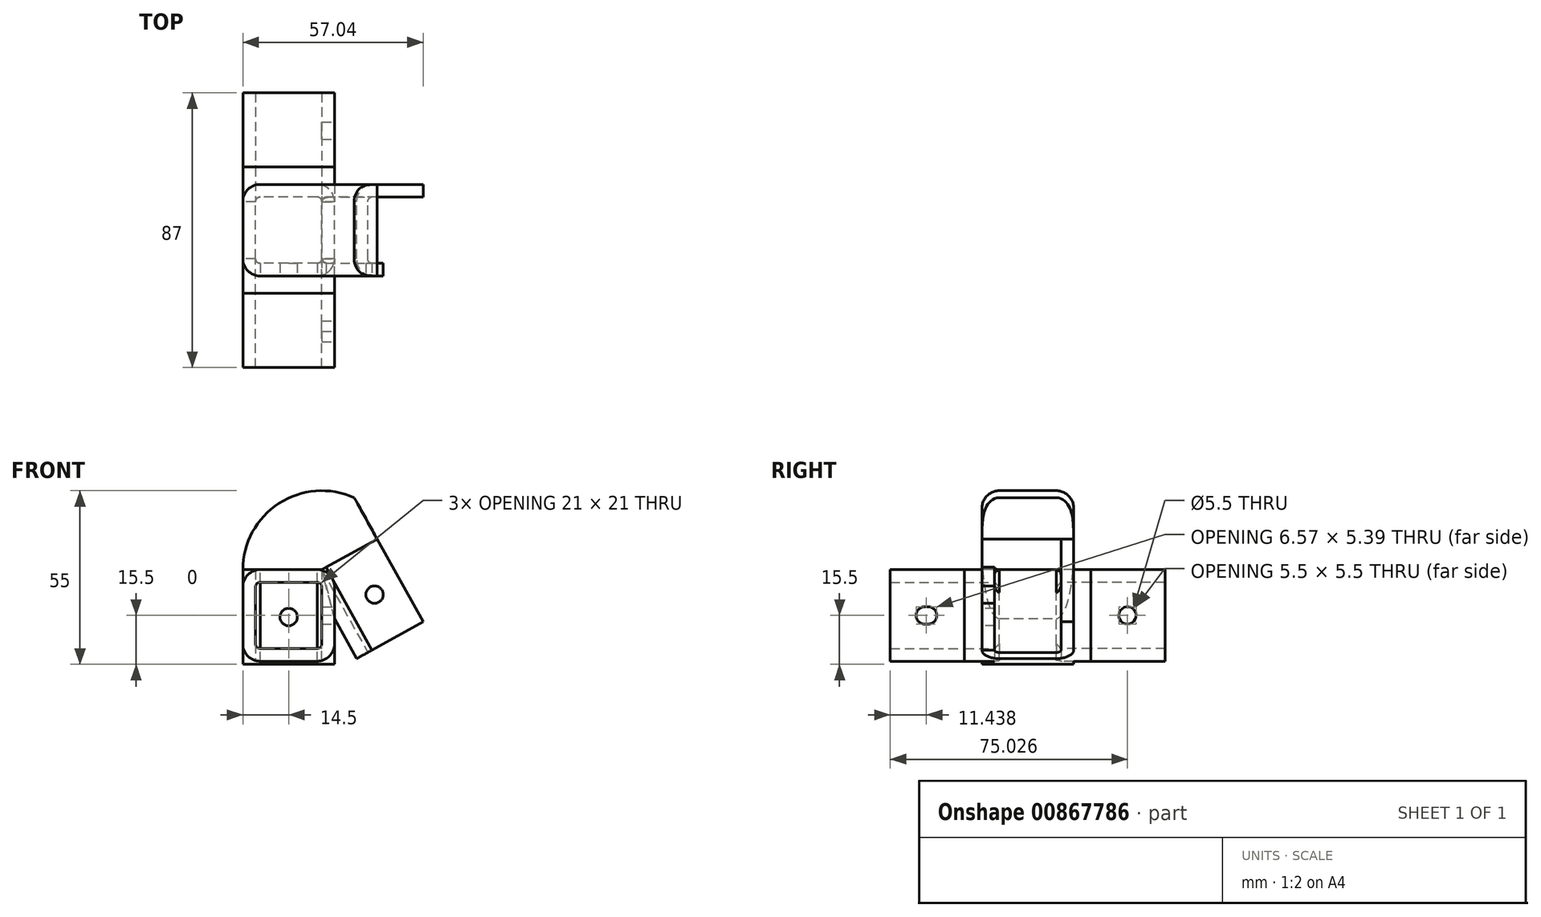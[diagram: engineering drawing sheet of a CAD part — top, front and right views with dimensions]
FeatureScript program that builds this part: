
annotation { "Feature Type Name" : "Feature", "Feature Type Description" : "" }
export const myFeature = defineFeature(function(context is Context, id is Id, definition is map)
    precondition{}
    {
        {
            var Q0;
            Q0=qCreatedBy(makeId("Top.planeOp"),FACE);
            var sketch = newSketch(context, id + "F0", { "sketchPlane" : qUnion([Q0])});
            skLineSegment(sketch, "E0.bottom", {"start": v(-1.5, 0) * mm, "end": v(-19.5, 0) * mm});
            skLineSegment(sketch, "E0.top", {"start": v(-1.5, 21) * mm, "end": v(-19.5, 21) * mm});
            skLineSegment(sketch, "E0.left", {"start": v(0, 1.5) * mm, "end": v(0, 19.5) * mm});
            skLineSegment(sketch, "E0.right", {"start": v(-21, 1.5) * mm, "end": v(-21, 19.5) * mm});
            skPoint(sketch, "E1.visualSharp", {"position": v(-21, 21) * mm});
            skArc(sketch, "E1.filletArc", {"start": v(-19.5, 21) * mm, "mid": v(-20.56, 20.56) * mm, "end": v(-21, 19.5) * mm});
            skPoint(sketch, "E2.visualSharp", {"position": v(0, 21) * mm});
            skArc(sketch, "E2.filletArc", {"start": v(0, 19.5) * mm, "mid": v(-0.44, 20.56) * mm, "end": v(-1.5, 21) * mm});
            skPoint(sketch, "E3.visualSharp", {"position": v(0, 0) * mm});
            skArc(sketch, "E3.filletArc", {"start": v(-1.5, 0) * mm, "mid": v(-0.44, 0.44) * mm, "end": v(0, 1.5) * mm});
            skPoint(sketch, "E4.visualSharp", {"position": v(-21, 0) * mm});
            skArc(sketch, "E4.filletArc", {"start": v(-21, 1.5) * mm, "mid": v(-20.56, 0.44) * mm, "end": v(-19.5, 0) * mm});
            skArc(sketch, "E5.0", {"start": v(4, 19.5) * mm, "mid": v(2.39, 23.39) * mm, "end": v(-1.5, 25) * mm});
            skLineSegment(sketch, "E5.1", {"start": v(4, 1.5) * mm, "end": v(4, 19.5) * mm});
            skLineSegment(sketch, "E5.2", {"start": v(-1.5, 25) * mm, "end": v(-19.5, 25) * mm});
            skArc(sketch, "E5.3", {"start": v(-1.5, -4) * mm, "mid": v(2.39, -2.39) * mm, "end": v(4, 1.5) * mm});
            skArc(sketch, "E5.4", {"start": v(-19.5, 25) * mm, "mid": v(-23.39, 23.39) * mm, "end": v(-25, 19.5) * mm});
            skLineSegment(sketch, "E5.5", {"start": v(-25, 1.5) * mm, "end": v(-25, 19.5) * mm});
            skArc(sketch, "E5.6", {"start": v(-25, 1.5) * mm, "mid": v(-23.39, -2.39) * mm, "end": v(-19.5, -4) * mm});
            skLineSegment(sketch, "E5.7", {"start": v(-1.5, -4) * mm, "end": v(-19.5, -4) * mm});
            skSolve(sketch);
        }
        {
            var Q0;
            Q0=makeQuery(id+"F0.imprint","IMPRINT",FACE,{"disambiguationData":[TD([[makeQuery(id+"F0.imprint","IMPRINT",EDGE,{"derivedFrom":sQuery(id+"F0.wireOp",EDGE,"E0.bottom")}),1.0]])]});
            extrude(context, id + "F1", {"entities" : qUnion([Q0]), "oppositeDirection" : true, "depth" : 30 * mm, "offsetDistance" : 25 * mm});
        }
        {
            var Q0;
            Q0=qCreatedBy(makeId("Front.planeOp"),FACE);
            var sketch = newSketch(context, id + "F2", { "sketchPlane" : qUnion([Q0])});
            skLineSegment(sketch, "E6", {"start": v(0, 0) * mm, "end": v(14.54, -26.24) * mm});
            skLineSegment(sketch, "E7", {"start": v(14.54, -26.24) * mm, "end": v(32.04, -16.54) * mm});
            skLineSegment(sketch, "E8", {"start": v(32.04, -16.54) * mm, "end": v(17.5, 9.7) * mm});
            skLineSegment(sketch, "E9", {"start": v(17.5, 9.7) * mm, "end": v(0, 0) * mm});
            skSolve(sketch);
        }
        {
            var Q0;
            Q0=makeQuery(id+"F2.imprint","IMPRINT",FACE,{"disambiguationData":[TD([[makeQuery(id+"F2.imprint","IMPRINT",EDGE,{"derivedFrom":sQuery(id+"F2.wireOp",EDGE,"E6")}),1.0]])]});
            extrude(context, id + "F3", {"entities" : qUnion([Q0]), "operationType" : NewBodyOperationType.ADD, "oppositeDirection" : true, "depth" : 21 * mm, "offsetDistance" : 25 * mm});
        }
        {
            var Q0;
            Q0=makeQuery(id+"F3.opExtrude","SWEPT_FACE",FACE,{"disambiguationData":[OSD([sQuery(id+"F2.wireOp",EDGE,"E7")])]});
            var sketch = newSketch(context, id + "F4", { "sketchPlane" : qUnion([Q0])});
            skLineSegment(sketch, "E10.bottom", {"start": v(20, 0) * mm, "end": v(1.5, 0) * mm});
            skLineSegment(sketch, "E10.top", {"start": v(20, -21) * mm, "end": v(1.5, -21) * mm});
            skLineSegment(sketch, "E10.left", {"start": v(20, 0) * mm, "end": v(20, -21) * mm});
            skLineSegment(sketch, "E10.right", {"start": v(0, -1.5) * mm, "end": v(0, -19.5) * mm});
            skPoint(sketch, "E11.visualSharp", {"position": v(0, 0) * mm});
            skArc(sketch, "E11.filletArc", {"start": v(1.5, 0) * mm, "mid": v(0.44, -0.44) * mm, "end": v(0, -1.5) * mm});
            skPoint(sketch, "E12.visualSharp", {"position": v(0, -21) * mm});
            skArc(sketch, "E12.filletArc", {"start": v(0, -19.5) * mm, "mid": v(0.44, -20.56) * mm, "end": v(1.5, -21) * mm});
            skLineSegment(sketch, "E13.0", {"start": v(20, -25) * mm, "end": v(1.5, -25) * mm});
            skLineSegment(sketch, "E13.1", {"start": v(20, 4) * mm, "end": v(1.5, 4) * mm});
            skArc(sketch, "E13.2", {"start": v(1.5, 4) * mm, "mid": v(-2.39, 2.39) * mm, "end": v(-4, -1.5) * mm});
            skLineSegment(sketch, "E13.3", {"start": v(-4, -1.5) * mm, "end": v(-4, -19.5) * mm});
            skArc(sketch, "E13.4", {"start": v(-4, -19.5) * mm, "mid": v(-2.39, -23.39) * mm, "end": v(1.5, -25) * mm});
            skLineSegment(sketch, "E14", {"start": v(20, 4) * mm, "end": v(20, 0) * mm});
            skLineSegment(sketch, "E15", {"start": v(20, -21) * mm, "end": v(20, -25) * mm});
            skSolve(sketch);
        }
        {
            var Q0;
            {var subQ0=sQuery(id+"F4.wireOp",EDGE,"E10.bottom");Q0=makeQuery(id+"F4.imprint","IMPRINT",FACE,{"disambiguationData":[TD([[makeQuery(id+"F4.imprint","IMPRINT",EDGE,{"derivedFrom":subQ0}),1.0]])]});}
            extrude(context, id + "F5", {"entities" : qUnion([Q0]), "operationType" : NewBodyOperationType.ADD, "oppositeDirection" : true, "depth" : 30 * mm, "offsetDistance" : 25 * mm});
        }
        {
            var Q0;
            {var subQ0=sQuery(id+"F2.wireOp",EDGE,"E7");Q0=makeQuery(id+"F5.boolean.opBoolean","MERGE",FACE,{"derivedFrom":[makeQuery(id+"F3.opExtrude","SWEPT_FACE",FACE,{"disambiguationData":[OSD([subQ0])]}),makeQuery(id+"F5.opExtrude","CAP_FACE",FACE,{"disambiguationData":[OSD([sQuery(id+"F2.wireOp",EDGE,"E6"),subQ0,sQuery(id+"F4.wireOp",EDGE,"E10.bottom"),sQuery(id+"F4.wireOp",EDGE,"E10.top"),sQuery(id+"F4.wireOp",EDGE,"E10.right"),sQuery(id+"F4.wireOp",EDGE,"E13.0"),sQuery(id+"F4.wireOp",EDGE,"E13.1"),sQuery(id+"F4.wireOp",EDGE,"E13.2"),sQuery(id+"F4.wireOp",EDGE,"E13.3"),sQuery(id+"F4.wireOp",EDGE,"E13.4"),sQuery(id+"F4.wireOp",EDGE,"E14"),sQuery(id+"F4.wireOp",EDGE,"E15")])],"isStart":true})]});}
            var sketch = newSketch(context, id + "F6", { "sketchPlane" : qUnion([Q0])});
            skLineSegment(sketch, "E16.bottom", {"start": v(20, 0) * mm, "end": v(1.5, 0) * mm});
            skLineSegment(sketch, "E16.top", {"start": v(20, -21) * mm, "end": v(1.5, -21) * mm});
            skLineSegment(sketch, "E16.left", {"start": v(20, 0) * mm, "end": v(20, -21) * mm});
            skLineSegment(sketch, "E16.right", {"start": v(0, -1.5) * mm, "end": v(0, -19.5) * mm});
            skPoint(sketch, "E17.visualSharp", {"position": v(0, 0) * mm});
            skArc(sketch, "E17.filletArc", {"start": v(1.5, 0) * mm, "mid": v(0.44, -0.44) * mm, "end": v(0, -1.5) * mm});
            skPoint(sketch, "E18.visualSharp", {"position": v(0, -21) * mm});
            skArc(sketch, "E18.filletArc", {"start": v(0, -19.5) * mm, "mid": v(0.44, -20.56) * mm, "end": v(1.5, -21) * mm});
            skSolve(sketch);
        }
        {
            var Q0;
            Q0=makeQuery(id+"F6.imprint","IMPRINT",FACE,{"disambiguationData":[TD([[makeQuery(id+"F6.imprint","IMPRINT",EDGE,{"derivedFrom":sQuery(id+"F6.wireOp",EDGE,"E16.bottom")}),1.0]])]});
            extrude(context, id + "F7", {"entities" : qUnion([Q0]), "operationType" : NewBodyOperationType.REMOVE, "oppositeDirection" : true, "depth" : 30 * mm, "offsetDistance" : 25 * mm});
        }
        {
            var Q0;
            Q0=makeQuery(id+"F1.opExtrude","CAP_FACE",FACE,{"disambiguationData":[OSD([sQuery(id+"F0.wireOp",EDGE,"E0.bottom"),sQuery(id+"F0.wireOp",EDGE,"E0.top"),sQuery(id+"F0.wireOp",EDGE,"E0.left"),sQuery(id+"F0.wireOp",EDGE,"E0.right"),sQuery(id+"F0.wireOp",EDGE,"E1.filletArc"),sQuery(id+"F0.wireOp",EDGE,"E2.filletArc"),sQuery(id+"F0.wireOp",EDGE,"E3.filletArc"),sQuery(id+"F0.wireOp",EDGE,"E4.filletArc"),sQuery(id+"F0.wireOp",EDGE,"E5.0"),sQuery(id+"F0.wireOp",EDGE,"E5.1"),sQuery(id+"F0.wireOp",EDGE,"E5.2"),sQuery(id+"F0.wireOp",EDGE,"E5.3"),sQuery(id+"F0.wireOp",EDGE,"E5.4"),sQuery(id+"F0.wireOp",EDGE,"E5.5"),sQuery(id+"F0.wireOp",EDGE,"E5.6"),sQuery(id+"F0.wireOp",EDGE,"E5.7")])],"isStart":true});
            var sketch = newSketch(context, id + "F8", { "sketchPlane" : qUnion([Q0])});
            skLineSegment(sketch, "E19.bottom", {"start": v(-19.5, 21) * mm, "end": v(-1.5, 21) * mm});
            skLineSegment(sketch, "E19.top", {"start": v(-19.5, 0) * mm, "end": v(-1.5, 0) * mm});
            skLineSegment(sketch, "E19.left", {"start": v(-21, 19.5) * mm, "end": v(-21, 1.5) * mm});
            skLineSegment(sketch, "E19.right", {"start": v(0, 19.5) * mm, "end": v(0, 1.5) * mm});
            skPoint(sketch, "E20.visualSharp", {"position": v(-21, 21) * mm});
            skArc(sketch, "E20.filletArc", {"start": v(-19.5, 21) * mm, "mid": v(-20.56, 20.56) * mm, "end": v(-21, 19.5) * mm});
            skPoint(sketch, "E21.visualSharp", {"position": v(0, 21) * mm});
            skArc(sketch, "E21.filletArc", {"start": v(0, 19.5) * mm, "mid": v(-0.44, 20.56) * mm, "end": v(-1.5, 21) * mm});
            skPoint(sketch, "E22.visualSharp", {"position": v(0, 0) * mm});
            skArc(sketch, "E22.filletArc", {"start": v(-1.5, 0) * mm, "mid": v(-0.44, 0.44) * mm, "end": v(0, 1.5) * mm});
            skPoint(sketch, "E23.visualSharp", {"position": v(-21, 0) * mm});
            skArc(sketch, "E23.filletArc", {"start": v(-21, 1.5) * mm, "mid": v(-20.56, 0.44) * mm, "end": v(-19.5, 0) * mm});
            skLineSegment(sketch, "E24.0", {"start": v(-19.5, 25) * mm, "end": v(-1.5, 25) * mm});
            skArc(sketch, "E24.1", {"start": v(4, 19.5) * mm, "mid": v(2.39, 23.39) * mm, "end": v(-1.5, 25) * mm});
            skArc(sketch, "E24.2", {"start": v(-19.5, 25) * mm, "mid": v(-23.39, 23.39) * mm, "end": v(-25, 19.5) * mm});
            skLineSegment(sketch, "E24.3", {"start": v(4, 19.5) * mm, "end": v(4, 1.5) * mm});
            skLineSegment(sketch, "E24.4", {"start": v(-25, 19.5) * mm, "end": v(-25, 1.5) * mm});
            skArc(sketch, "E24.5", {"start": v(-25, 1.5) * mm, "mid": v(-23.39, -2.39) * mm, "end": v(-19.5, -4) * mm});
            skLineSegment(sketch, "E24.6", {"start": v(-19.5, -4) * mm, "end": v(-1.5, -4) * mm});
            skArc(sketch, "E24.7", {"start": v(-1.5, -4) * mm, "mid": v(2.39, -2.39) * mm, "end": v(4, 1.5) * mm});
            skLineSegment(sketch, "E25", {"start": v(0, 24.8) * mm, "end": v(0, -3.8) * mm});
            skSolve(sketch);
        }
        {
            var Q0;
            Q0=makeQuery(id+"F8.imprint","IMPRINT",FACE,{"disambiguationData":[TD([[makeQuery(id+"F8.imprint","IMPRINT",EDGE,{"derivedFrom":sQuery(id+"F8.wireOp",EDGE,"E19.bottom")}),-1.0]])]});
            var Q1;
            Q1=makeQuery(id+"F8.imprint","IMPRINT",FACE,{"disambiguationData":[TD([[makeQuery(id+"F8.imprint","IMPRINT",EDGE,{"derivedFrom":sQuery(id+"F8.wireOp",EDGE,"E19.bottom")}),1.0]])]});
            var Q2;
            Q2=sQuery(id+"F8.wireOp",EDGE,"E19.right");
            revolve(context, id + "F9", {"surfaceOperationType" : NewSurfaceOperationType.NEW, "entities" : qUnion([Q0, Q1]), "axis" : qUnion([Q2]), "revolveType" : RevolveType.ONE_DIRECTION, "oppositeDirection" : true, "angle" : 151 * degree});
        }
        {
            var Q0;
            Q0=makeQuery(id+"F9.opRevolve","SWEPT_FACE",FACE,{"disambiguationData":[OSD([sQuery(id+"F8.wireOp",EDGE,"E24.0")])]});
            var sketch = newSketch(context, id + "F10", { "sketchPlane" : qUnion([Q0])});
            skLineSegment(sketch, "E26", {"start": v(-14.13, 7.84) * mm, "end": v(-17.5, 9.7) * mm});
            skLineSegment(sketch, "E27", {"start": v(-17.5, 9.7) * mm, "end": v(-9, 25.03) * mm});
            skLineSegment(sketch, "E28", {"start": v(-9, 25.03) * mm, "end": v(-34.12, 7.75) * mm});
            skLineSegment(sketch, "E29", {"start": v(-34.12, 7.75) * mm, "end": v(-17.5, 9.7) * mm});
            skSolve(sketch);
        }
        {
            var Q0;
            Q0=makeQuery(id+"F10.imprint","IMPRINT",FACE,{"disambiguationData":[TD([[makeQuery(id+"F10.imprint","IMPRINT",EDGE,{"derivedFrom":sQuery(id+"F10.wireOp",EDGE,"E27")}),1.0]])]});
            extrude(context, id + "F11", {"entities" : qUnion([Q0]), "operationType" : NewBodyOperationType.REMOVE, "oppositeDirection" : true, "depth" : 41 * mm, "offsetDistance" : 25 * mm});
        }
        {
            var Q0;
            Q0=makeQuery(id+"F1.opExtrude","CAP_FACE",FACE,{"disambiguationData":[OSD([sQuery(id+"F0.wireOp",EDGE,"E0.bottom"),sQuery(id+"F0.wireOp",EDGE,"E0.top"),sQuery(id+"F0.wireOp",EDGE,"E0.left"),sQuery(id+"F0.wireOp",EDGE,"E0.right"),sQuery(id+"F0.wireOp",EDGE,"E1.filletArc"),sQuery(id+"F0.wireOp",EDGE,"E2.filletArc"),sQuery(id+"F0.wireOp",EDGE,"E3.filletArc"),sQuery(id+"F0.wireOp",EDGE,"E4.filletArc"),sQuery(id+"F0.wireOp",EDGE,"E5.0"),sQuery(id+"F0.wireOp",EDGE,"E5.1"),sQuery(id+"F0.wireOp",EDGE,"E5.2"),sQuery(id+"F0.wireOp",EDGE,"E5.3"),sQuery(id+"F0.wireOp",EDGE,"E5.4"),sQuery(id+"F0.wireOp",EDGE,"E5.5"),sQuery(id+"F0.wireOp",EDGE,"E5.6"),sQuery(id+"F0.wireOp",EDGE,"E5.7")])],"isStart":false});
            var sketch = newSketch(context, id + "F12", { "sketchPlane" : qUnion([Q0])});
            skLineSegment(sketch, "E30.bottom", {"start": v(-1.5, -21) * mm, "end": v(-9, -21) * mm});
            skLineSegment(sketch, "E30.top", {"start": v(-1.5, 0) * mm, "end": v(-9, 0) * mm});
            skLineSegment(sketch, "E30.left", {"start": v(0, -19.5) * mm, "end": v(0, -1.5) * mm});
            skLineSegment(sketch, "E30.right", {"start": v(-10.5, -19.5) * mm, "end": v(-10.5, -1.5) * mm});
            skPoint(sketch, "E31.visualSharp", {"position": v(0, -21) * mm});
            skArc(sketch, "E31.filletArc", {"start": v(-1.5, -21) * mm, "mid": v(-0.44, -20.56) * mm, "end": v(0, -19.5) * mm});
            skPoint(sketch, "E32.visualSharp", {"position": v(-10.5, -21) * mm});
            skArc(sketch, "E32.filletArc", {"start": v(-10.5, -19.5) * mm, "mid": v(-10.06, -20.56) * mm, "end": v(-9, -21) * mm});
            skPoint(sketch, "E33.visualSharp", {"position": v(-10.5, 0) * mm});
            skArc(sketch, "E33.filletArc", {"start": v(-9, 0) * mm, "mid": v(-10.06, -0.44) * mm, "end": v(-10.5, -1.5) * mm});
            skPoint(sketch, "E34.visualSharp", {"position": v(0, 0) * mm});
            skArc(sketch, "E34.filletArc", {"start": v(0, -1.5) * mm, "mid": v(-0.44, -0.44) * mm, "end": v(-1.5, 0) * mm});
            skSolve(sketch);
        }
        {
            var Q0;
            Q0=makeQuery(id+"F12.imprint","IMPRINT",FACE,{"disambiguationData":[TD([[makeQuery(id+"F12.imprint","IMPRINT",EDGE,{"derivedFrom":sQuery(id+"F12.wireOp",EDGE,"E30.bottom")}),-1.0]])]});
            extrude(context, id + "F13", {"entities" : qUnion([Q0]), "operationType" : NewBodyOperationType.REMOVE, "oppositeDirection" : true, "depth" : 28 * mm, "offsetDistance" : 25 * mm});
        }
        {
            var Q0;
            Q0=makeQuery(id+"F5.opExtrude","SWEPT_FACE",FACE,{"disambiguationData":[OSD([sQuery(id+"F4.wireOp",EDGE,"E13.1")])]});
            var sketch = newSketch(context, id + "F14", { "sketchPlane" : qUnion([Q0])});
            skLineSegment(sketch, "E35", {"start": v(9.4, 5.21) * mm, "end": v(23.95, -21.03) * mm});
            skCircle(sketch, "E36", {"center": v(16.67, -7.9) * mm, "radius": 2.75 * mm});
            skSolve(sketch);
        }
        {
            var Q0;
            {var subQ0=sQuery(id+"F14.wireOp",EDGE,"E36");var subQ1=sQuery(id+"F14.wireOp",EDGE,"E35");var subQ2=makeQuery(id+"F14.imprint","INTERSECT",VERTEX,{"disambiguationData":[OD(0.0)],"derivedFrom":[subQ1,subQ0]});Q0=makeQuery(id+"F14.imprint","IMPRINT",FACE,{"disambiguationData":[TD([[makeQuery(id+"F14.imprint","IMPRINT",EDGE,{"disambiguationData":[TD([[subQ2,-1.0]])],"derivedFrom":subQ1}),1.0]])]});}
            var Q1;
            {var subQ0=sQuery(id+"F14.wireOp",EDGE,"E36");var subQ1=sQuery(id+"F14.wireOp",EDGE,"E35");var subQ2=makeQuery(id+"F14.imprint","INTERSECT",VERTEX,{"disambiguationData":[OD(0.0)],"derivedFrom":[subQ1,subQ0]});Q1=makeQuery(id+"F14.imprint","IMPRINT",FACE,{"disambiguationData":[TD([[makeQuery(id+"F14.imprint","IMPRINT",EDGE,{"disambiguationData":[TD([[subQ2,-1.0]])],"derivedFrom":subQ1}),-1.0]])]});}
            extrude(context, id + "F15", {"entities" : qUnion([Q0, Q1]), "operationType" : NewBodyOperationType.REMOVE, "oppositeDirection" : true, "depth" : 25 * mm, "offsetDistance" : 25 * mm});
        }
        {
            var Q0;
            Q0=makeQuery(id+"F1.opExtrude","SWEPT_FACE",FACE,{"disambiguationData":[OSD([sQuery(id+"F0.wireOp",EDGE,"E5.7")])]});
            var sketch = newSketch(context, id + "F16", { "sketchPlane" : qUnion([Q0])});
            skLineSegment(sketch, "E37", {"start": v(-10.5, 0) * mm, "end": v(-10.5, -30) * mm});
            skCircle(sketch, "E38", {"center": v(-10.5, -15) * mm, "radius": 2.75 * mm});
            skSolve(sketch);
        }
        {
            var Q0;
            {var subQ0=sQuery(id+"F16.wireOp",EDGE,"E38");var subQ1=sQuery(id+"F16.wireOp",EDGE,"E37");var subQ2=makeQuery(id+"F16.imprint","INTERSECT",VERTEX,{"disambiguationData":[OD(0.0)],"derivedFrom":[subQ1,subQ0]});Q0=makeQuery(id+"F16.imprint","IMPRINT",FACE,{"disambiguationData":[TD([[makeQuery(id+"F16.imprint","IMPRINT",EDGE,{"disambiguationData":[TD([[subQ2,-1.0]])],"derivedFrom":subQ1}),1.0]])]});}
            var Q1;
            {var subQ0=sQuery(id+"F16.wireOp",EDGE,"E38");var subQ1=sQuery(id+"F16.wireOp",EDGE,"E37");var subQ2=makeQuery(id+"F16.imprint","INTERSECT",VERTEX,{"disambiguationData":[OD(0.0)],"derivedFrom":[subQ1,subQ0]});Q1=makeQuery(id+"F16.imprint","IMPRINT",FACE,{"disambiguationData":[TD([[makeQuery(id+"F16.imprint","IMPRINT",EDGE,{"disambiguationData":[TD([[subQ2,-1.0]])],"derivedFrom":subQ1}),-1.0]])]});}
            extrude(context, id + "F17", {"entities" : qUnion([Q0, Q1]), "operationType" : NewBodyOperationType.REMOVE, "oppositeDirection" : true, "depth" : 10 * mm, "offsetDistance" : 25 * mm});
        }
        {
            var Q0;
            Q0=makeQuery(id+"F1.opExtrude","SWEPT_FACE",FACE,{"disambiguationData":[OSD([sQuery(id+"F0.wireOp",EDGE,"E5.2")])]});
            var sketch = newSketch(context, id + "F18", { "sketchPlane" : qUnion([Q0])});
            skLineSegment(sketch, "E39", {"start": v(23.9, -29) * mm, "end": v(25, -29) * mm});
            skLineSegment(sketch, "E40.bottom", {"start": v(19.5, -29) * mm, "end": v(1.5, -29) * mm});
            skLineSegment(sketch, "E40.top", {"start": v(19.5, 0) * mm, "end": v(1.5, 0) * mm});
            skLineSegment(sketch, "E40.left", {"start": v(25, -23.5) * mm, "end": v(25, -5.5) * mm});
            skLineSegment(sketch, "E40.right", {"start": v(-4, -23.5) * mm, "end": v(-4, -5.5) * mm});
            skPoint(sketch, "E41.visualSharp", {"position": v(-4, 0) * mm});
            skArc(sketch, "E41.filletArc", {"start": v(1.5, 0) * mm, "mid": v(-2.39, -1.61) * mm, "end": v(-4, -5.5) * mm});
            skPoint(sketch, "E42.visualSharp", {"position": v(25, 0) * mm});
            skArc(sketch, "E42.filletArc", {"start": v(25, -5.5) * mm, "mid": v(23.39, -1.61) * mm, "end": v(19.5, 0) * mm});
            skPoint(sketch, "E43.visualSharp", {"position": v(25, -29) * mm});
            skArc(sketch, "E43.filletArc", {"start": v(19.5, -29) * mm, "mid": v(23.39, -27.39) * mm, "end": v(25, -23.5) * mm});
            skPoint(sketch, "E44.visualSharp", {"position": v(-4, -29) * mm});
            skArc(sketch, "E44.filletArc", {"start": v(-4, -23.5) * mm, "mid": v(-2.39, -27.39) * mm, "end": v(1.5, -29) * mm});
            skLineSegment(sketch, "E45.0", {"start": v(19.5, -4) * mm, "end": v(1.5, -4) * mm});
            skArc(sketch, "E45.1", {"start": v(21, -5.5) * mm, "mid": v(20.56, -4.44) * mm, "end": v(19.5, -4) * mm});
            skArc(sketch, "E45.2", {"start": v(1.5, -4) * mm, "mid": v(0.44, -4.44) * mm, "end": v(0, -5.5) * mm});
            skLineSegment(sketch, "E45.3", {"start": v(21, -23.5) * mm, "end": v(21, -5.5) * mm});
            skLineSegment(sketch, "E45.4", {"start": v(0, -23.5) * mm, "end": v(0, -5.5) * mm});
            skArc(sketch, "E45.5", {"start": v(0, -23.5) * mm, "mid": v(0.44, -24.56) * mm, "end": v(1.5, -25) * mm});
            skLineSegment(sketch, "E45.6", {"start": v(19.5, -25) * mm, "end": v(1.5, -25) * mm});
            skArc(sketch, "E45.7", {"start": v(19.5, -25) * mm, "mid": v(20.56, -24.56) * mm, "end": v(21, -23.5) * mm});
            skSolve(sketch);
        }
        {
            var Q0;
            Q0=makeQuery(id+"F18.imprint","IMPRINT",FACE,{"disambiguationData":[TD([[makeQuery(id+"F18.imprint","IMPRINT",EDGE,{"derivedFrom":sQuery(id+"F18.wireOp",EDGE,"E40.right")}),-1.0]])]});
            var Q1;
            {var subQ0=sQuery(id+"F18.wireOp",EDGE,"E40.top");Q1=makeQuery(id+"F18.imprint","IMPRINT",FACE,{"disambiguationData":[TD([[makeQuery(id+"F18.imprint","IMPRINT",EDGE,{"derivedFrom":subQ0}),-1.0]])]});}
            var Q2;
            Q2=makeQuery(id+"F18.imprint","IMPRINT",FACE,{"disambiguationData":[TD([[makeQuery(id+"F18.imprint","IMPRINT",EDGE,{"derivedFrom":sQuery(id+"F18.wireOp",EDGE,"E40.left")}),1.0]])]});
            var Q3;
            {var subQ0=sQuery(id+"F18.wireOp",EDGE,"E40.bottom");Q3=makeQuery(id+"F18.imprint","IMPRINT",FACE,{"disambiguationData":[TD([[makeQuery(id+"F18.imprint","IMPRINT",EDGE,{"derivedFrom":subQ0}),-1.0]])]});}
            extrude(context, id + "F19", {"entities" : qUnion([Q0, Q1, Q2, Q3]), "endBound" : BoundingType.SYMMETRIC, "depth" : 11 * mm, "offsetDistance" : 25 * mm});
        }
        {
            var Q0;
            Q0=makeQuery(id+"F1.opExtrude","CAP_FACE",FACE,{"disambiguationData":[OSD([sQuery(id+"F0.wireOp",EDGE,"E0.bottom"),sQuery(id+"F0.wireOp",EDGE,"E0.top"),sQuery(id+"F0.wireOp",EDGE,"E0.left"),sQuery(id+"F0.wireOp",EDGE,"E0.right"),sQuery(id+"F0.wireOp",EDGE,"E1.filletArc"),sQuery(id+"F0.wireOp",EDGE,"E2.filletArc"),sQuery(id+"F0.wireOp",EDGE,"E3.filletArc"),sQuery(id+"F0.wireOp",EDGE,"E4.filletArc"),sQuery(id+"F0.wireOp",EDGE,"E5.0"),sQuery(id+"F0.wireOp",EDGE,"E5.1"),sQuery(id+"F0.wireOp",EDGE,"E5.2"),sQuery(id+"F0.wireOp",EDGE,"E5.3"),sQuery(id+"F0.wireOp",EDGE,"E5.4"),sQuery(id+"F0.wireOp",EDGE,"E5.5"),sQuery(id+"F0.wireOp",EDGE,"E5.6"),sQuery(id+"F0.wireOp",EDGE,"E5.7")])],"isStart":false});
            var sketch = newSketch(context, id + "F20", { "sketchPlane" : qUnion([Q0])});
            skLineSegment(sketch, "E46", {"start": v(-1.5, -21) * mm, "end": v(-19.5, -21) * mm});
            skLineSegment(sketch, "E47", {"start": v(-21, -19.5) * mm, "end": v(-21, -1.5) * mm});
            skLineSegment(sketch, "E48", {"start": v(-19.5, 0) * mm, "end": v(-1.5, 0) * mm});
            skLineSegment(sketch, "E49", {"start": v(0, -1.5) * mm, "end": v(0, -19.5) * mm});
            skPoint(sketch, "E50.visualSharp", {"position": v(0, -21) * mm});
            skArc(sketch, "E50.filletArc", {"start": v(-1.5, -21) * mm, "mid": v(-0.44, -20.56) * mm, "end": v(0, -19.5) * mm});
            skPoint(sketch, "E51.visualSharp", {"position": v(-21, -21) * mm});
            skArc(sketch, "E51.filletArc", {"start": v(-21, -19.5) * mm, "mid": v(-20.56, -20.56) * mm, "end": v(-19.5, -21) * mm});
            skPoint(sketch, "E52.visualSharp", {"position": v(-21, 0) * mm});
            skArc(sketch, "E52.filletArc", {"start": v(-19.5, 0) * mm, "mid": v(-20.56, -0.44) * mm, "end": v(-21, -1.5) * mm});
            skPoint(sketch, "E53.visualSharp", {"position": v(0, 0) * mm});
            skArc(sketch, "E53.filletArc", {"start": v(0, -1.5) * mm, "mid": v(-0.44, -0.44) * mm, "end": v(-1.5, 0) * mm});
            skSolve(sketch);
        }
        {
            var Q0;
            Q0=makeQuery(id+"F20.imprint","IMPRINT",FACE,{"disambiguationData":[TD([[makeQuery(id+"F20.imprint","IMPRINT",EDGE,{"derivedFrom":sQuery(id+"F20.wireOp",EDGE,"E46")}),-1.0]])]});
            extrude(context, id + "F21", {"entities" : qUnion([Q0]), "operationType" : NewBodyOperationType.REMOVE, "oppositeDirection" : true, "depth" : 30 * mm, "offsetDistance" : 25 * mm});
        }
        {
            var Q0;
            {var subQ0=sQuery(id+"F2.wireOp",EDGE,"E7");Q0=makeQuery(id+"F5.boolean.opBoolean","MERGE",FACE,{"derivedFrom":[makeQuery(id+"F3.opExtrude","SWEPT_FACE",FACE,{"disambiguationData":[OSD([subQ0])]}),makeQuery(id+"F5.opExtrude","CAP_FACE",FACE,{"disambiguationData":[OSD([sQuery(id+"F2.wireOp",EDGE,"E6"),subQ0,sQuery(id+"F4.wireOp",EDGE,"E10.bottom"),sQuery(id+"F4.wireOp",EDGE,"E10.top"),sQuery(id+"F4.wireOp",EDGE,"E10.right"),sQuery(id+"F4.wireOp",EDGE,"E13.0"),sQuery(id+"F4.wireOp",EDGE,"E13.1"),sQuery(id+"F4.wireOp",EDGE,"E13.2"),sQuery(id+"F4.wireOp",EDGE,"E13.3"),sQuery(id+"F4.wireOp",EDGE,"E13.4"),sQuery(id+"F4.wireOp",EDGE,"E14"),sQuery(id+"F4.wireOp",EDGE,"E15")])],"isStart":true})]});}
            var sketch = newSketch(context, id + "F22", { "sketchPlane" : qUnion([Q0])});
            skLineSegment(sketch, "E54", {"start": v(1.5, -21) * mm, "end": v(1.5, -21) * mm});
            skLineSegment(sketch, "E55", {"start": v(0, -19.5) * mm, "end": v(0, -19.5) * mm});
            skPoint(sketch, "E56.visualSharp", {"position": v(0, -21) * mm});
            skArc(sketch, "E56.filletArc", {"start": v(0, -19.5) * mm, "mid": v(0.44, -20.56) * mm, "end": v(1.5, -21) * mm});
            skLineSegment(sketch, "E57", {"start": v(0, -19.5) * mm, "end": v(3.05, -19.5) * mm});
            skLineSegment(sketch, "E58", {"start": v(3.05, -19.5) * mm, "end": v(3.05, -21) * mm});
            skLineSegment(sketch, "E59", {"start": v(3.05, -21) * mm, "end": v(1.5, -21) * mm});
            skSolve(sketch);
        }
        {
            var Q0;
            Q0=makeQuery(id+"F22.imprint","IMPRINT",FACE,{"disambiguationData":[TD([[makeQuery(id+"F22.imprint","IMPRINT",EDGE,{"derivedFrom":sQuery(id+"F22.wireOp",EDGE,"HInRQnyC-sIoa-7sX4-uU5k-RffJmijH44JD")}),-1.0]])]});
            var Q1;
            Q1=makeQuery(id+"F22.imprint","IMPRINT",FACE,{"disambiguationData":[TD([[makeQuery(id+"F22.imprint","IMPRINT",EDGE,{"derivedFrom":sQuery(id+"F22.wireOp",EDGE,"E56.filletArc")}),1.0]])]});
            extrude(context, id + "F23", {"entities" : qUnion([Q0, Q1]), "operationType" : NewBodyOperationType.REMOVE, "oppositeDirection" : true, "depth" : 30 * mm, "offsetDistance" : 25 * mm});
        }
        {
            var Q0;
            Q0=makeQuery(id+"F19.opExtrude","CAP_FACE",FACE,{"disambiguationData":[OSD([sQuery(id+"F18.wireOp",EDGE,"E40.bottom"),sQuery(id+"F18.wireOp",EDGE,"E40.top"),sQuery(id+"F18.wireOp",EDGE,"E40.left"),sQuery(id+"F18.wireOp",EDGE,"E40.right"),sQuery(id+"F18.wireOp",EDGE,"E41.filletArc"),sQuery(id+"F18.wireOp",EDGE,"E42.filletArc"),sQuery(id+"F18.wireOp",EDGE,"E43.filletArc"),sQuery(id+"F18.wireOp",EDGE,"E44.filletArc"),sQuery(id+"F18.wireOp",EDGE,"E45.0"),sQuery(id+"F18.wireOp",EDGE,"E45.1"),sQuery(id+"F18.wireOp",EDGE,"E45.2"),sQuery(id+"F18.wireOp",EDGE,"E45.3"),sQuery(id+"F18.wireOp",EDGE,"E45.4"),sQuery(id+"F18.wireOp",EDGE,"E45.5"),sQuery(id+"F18.wireOp",EDGE,"E45.6"),sQuery(id+"F18.wireOp",EDGE,"E45.7")])],"isStart":false});
            var sketch = newSketch(context, id + "F24", { "sketchPlane" : qUnion([Q0])});
            skLineSegment(sketch, "E60", {"start": v(22.66, -29) * mm, "end": v(25, -29) * mm});
            skLineSegment(sketch, "E61.bottom", {"start": v(19.5, -29) * mm, "end": v(1.5, -29) * mm});
            skLineSegment(sketch, "E61.top", {"start": v(19.5, 0) * mm, "end": v(1.5, 0) * mm});
            skLineSegment(sketch, "E61.left", {"start": v(25, -23.5) * mm, "end": v(25, -5.5) * mm});
            skLineSegment(sketch, "E61.right", {"start": v(-4, -23.5) * mm, "end": v(-4, -5.5) * mm});
            skPoint(sketch, "E62.visualSharp", {"position": v(-4, 0) * mm});
            skArc(sketch, "E62.filletArc", {"start": v(1.5, 0) * mm, "mid": v(-2.39, -1.61) * mm, "end": v(-4, -5.5) * mm});
            skPoint(sketch, "E63.visualSharp", {"position": v(25, 0) * mm});
            skArc(sketch, "E63.filletArc", {"start": v(25, -5.5) * mm, "mid": v(23.39, -1.61) * mm, "end": v(19.5, 0) * mm});
            skPoint(sketch, "E64.visualSharp", {"position": v(25, -29) * mm});
            skArc(sketch, "E64.filletArc", {"start": v(19.5, -29) * mm, "mid": v(23.39, -27.39) * mm, "end": v(25, -23.5) * mm});
            skPoint(sketch, "E65.visualSharp", {"position": v(-4, -29) * mm});
            skArc(sketch, "E65.filletArc", {"start": v(-4, -23.5) * mm, "mid": v(-2.39, -27.39) * mm, "end": v(1.5, -29) * mm});
            skLineSegment(sketch, "E66.0", {"start": v(19.5, -4) * mm, "end": v(1.5, -4) * mm});
            skArc(sketch, "E66.1", {"start": v(21, -5.5) * mm, "mid": v(20.56, -4.44) * mm, "end": v(19.5, -4) * mm});
            skArc(sketch, "E66.2", {"start": v(1.5, -4) * mm, "mid": v(0.44, -4.44) * mm, "end": v(0, -5.5) * mm});
            skLineSegment(sketch, "E66.3", {"start": v(21, -23.5) * mm, "end": v(21, -5.5) * mm});
            skLineSegment(sketch, "E66.4", {"start": v(0, -23.5) * mm, "end": v(0, -5.5) * mm});
            skArc(sketch, "E66.5", {"start": v(0, -23.5) * mm, "mid": v(0.44, -24.56) * mm, "end": v(1.5, -25) * mm});
            skLineSegment(sketch, "E66.6", {"start": v(19.5, -25) * mm, "end": v(1.5, -25) * mm});
            skArc(sketch, "E66.7", {"start": v(19.5, -25) * mm, "mid": v(20.56, -24.56) * mm, "end": v(21, -23.5) * mm});
            skSolve(sketch);
        }
        {
            var Q0;
            Q0=makeQuery(id+"F24.imprint","IMPRINT",FACE,{"disambiguationData":[TD([[makeQuery(id+"F24.imprint","IMPRINT",EDGE,{"derivedFrom":sQuery(id+"F24.wireOp",EDGE,"E61.bottom")}),-1.0]])]});
            extrude(context, id + "F25", {"entities" : qUnion([Q0]), "depth" : 23.5 * mm, "offsetDistance" : 25 * mm});
        }
        {
            var Q0;
            Q0=makeQuery(id+"F25.boolean.opBoolean","MERGE",FACE,{"derivedFrom":[makeQuery(id+"F19.boolean.opBoolean","MERGE",FACE,{"derivedFrom":[makeQuery(id+"F1.opExtrude","SWEPT_FACE",FACE,{"disambiguationData":[OSD([sQuery(id+"F0.wireOp",EDGE,"E5.1")])]}),makeQuery(id+"F19.opExtrude","SWEPT_FACE",FACE,{"disambiguationData":[OSD([sQuery(id+"F18.wireOp",EDGE,"E40.right")])]})]}),makeQuery(id+"F25.opExtrude","SWEPT_FACE",FACE,{"disambiguationData":[OSD([sQuery(id+"F24.wireOp",EDGE,"E61.right")])]})]});
            var sketch = newSketch(context, id + "F26", { "sketchPlane" : qUnion([Q0])});
            skCircle(sketch, "E67", {"center": v(42.03, -14.5) * mm, "radius": 2.75 * mm});
            skPoint(sketch, "E67.centerSnap0", {"position": v(54, -14.5) * mm});
            skSolve(sketch);
        }
        {
            var Q0;
            Q0=makeQuery(id+"F26.imprint","IMPRINT",FACE,{"disambiguationData":[TD([[makeQuery(id+"F26.imprint","IMPRINT",EDGE,{"derivedFrom":sQuery(id+"F26.wireOp",EDGE,"E67")}),1.0]])]});
            extrude(context, id + "F27", {"entities" : qUnion([Q0]), "operationType" : NewBodyOperationType.REMOVE, "oppositeDirection" : true, "depth" : 17 * mm, "offsetDistance" : 25 * mm});
        }
        {
            var Q0;
            Q0=qCreatedBy(makeId("Front.planeOp"),FACE);
            cPlane(context, id + "F28", {"entities" : qUnion([Q0]), "cplaneType" : CPlaneType.OFFSET, "offset" : (21 / 2) * mm, "oppositeDirection" : true, "width" : 150 * mm, "height" : 150 * mm});
        }
        {
            var Q0;
            Q0=makeQuery(id+"F19.opExtrude","SWEPT_BODY",BODY,{"disambiguationData":[OSD([sQuery(id+"F18.wireOp",EDGE,"E40.bottom"),sQuery(id+"F18.wireOp",EDGE,"E40.top"),sQuery(id+"F18.wireOp",EDGE,"E40.left"),sQuery(id+"F18.wireOp",EDGE,"E40.right"),sQuery(id+"F18.wireOp",EDGE,"E41.filletArc"),sQuery(id+"F18.wireOp",EDGE,"E42.filletArc"),sQuery(id+"F18.wireOp",EDGE,"E43.filletArc"),sQuery(id+"F18.wireOp",EDGE,"E44.filletArc"),sQuery(id+"F18.wireOp",EDGE,"E45.0"),sQuery(id+"F18.wireOp",EDGE,"E45.1"),sQuery(id+"F18.wireOp",EDGE,"E45.2"),sQuery(id+"F18.wireOp",EDGE,"E45.3"),sQuery(id+"F18.wireOp",EDGE,"E45.4"),sQuery(id+"F18.wireOp",EDGE,"E45.5"),sQuery(id+"F18.wireOp",EDGE,"E45.6"),sQuery(id+"F18.wireOp",EDGE,"E45.7")])]});
            var Q1;
            Q1=makeQuery(id+"F25.opExtrude","SWEPT_BODY",BODY,{"disambiguationData":[OSD([sQuery(id+"F24.wireOp",EDGE,"E61.bottom"),sQuery(id+"F24.wireOp",EDGE,"E61.top"),sQuery(id+"F24.wireOp",EDGE,"E61.left"),sQuery(id+"F24.wireOp",EDGE,"E61.right"),sQuery(id+"F24.wireOp",EDGE,"E62.filletArc"),sQuery(id+"F24.wireOp",EDGE,"E63.filletArc"),sQuery(id+"F24.wireOp",EDGE,"E64.filletArc"),sQuery(id+"F24.wireOp",EDGE,"E65.filletArc"),sQuery(id+"F24.wireOp",EDGE,"E66.0"),sQuery(id+"F24.wireOp",EDGE,"E66.1"),sQuery(id+"F24.wireOp",EDGE,"E66.2"),sQuery(id+"F24.wireOp",EDGE,"E66.3"),sQuery(id+"F24.wireOp",EDGE,"E66.4"),sQuery(id+"F24.wireOp",EDGE,"E66.5"),sQuery(id+"F24.wireOp",EDGE,"E66.6"),sQuery(id+"F24.wireOp",EDGE,"E66.7")])]});
            var Q2;
            Q2=qCreatedBy(id+"F28.planeOp",FACE);
            mirror(context, id + "F29", {"entities" : qUnion([Q0, Q1]), "mirrorPlane" : qUnion([Q2])});
        }
        {
            var Q0;
            Q0=makeQuery(id+"F25.opExtrude","SWEPT_FACE",FACE,{"disambiguationData":[OSD([sQuery(id+"F24.wireOp",EDGE,"E61.right")])]});
            var sketch = newSketch(context, id + "F30", { "sketchPlane" : qUnion([Q0])});
            skCircle(sketch, "E68", {"center": v(42.02, -14.5) * mm, "radius": 2.75 * mm});
            skPoint(sketch, "E68.centerSnap0", {"position": v(54, -14.5) * mm});
            skSolve(sketch);
        }
        {
            var Q0;
            Q0=makeQuery(id+"F30.imprint","IMPRINT",FACE,{"disambiguationData":[TD([[makeQuery(id+"F30.imprint","IMPRINT",EDGE,{"derivedFrom":sQuery(id+"F30.wireOp",EDGE,"E68")}),1.0]])]});
            extrude(context, id + "F31", {"entities" : qUnion([Q0]), "operationType" : NewBodyOperationType.REMOVE, "oppositeDirection" : true, "depth" : 5 * mm, "offsetDistance" : 25 * mm});
        }
        {
            var Q0;
            Q0=makeQuery(id+"F29.opPattern","COPY",FACE,{"derivedFrom":makeQuery(id+"F25.opExtrude","SWEPT_FACE",FACE,{"disambiguationData":[OSD([sQuery(id+"F24.wireOp",EDGE,"E61.right")])]}),"instanceName":"1"});
            var sketch = newSketch(context, id + "F32", { "sketchPlane" : qUnion([Q0])});
            skCircle(sketch, "E69", {"center": v(-22.1, -14.5) * mm, "radius": 2.75 * mm});
            skPoint(sketch, "E69.centerSnap0", {"position": v(-33, -14.5) * mm});
            skSolve(sketch);
        }
        {
            var Q0;
            Q0=makeQuery(id+"F32.imprint","IMPRINT",FACE,{"disambiguationData":[TD([[makeQuery(id+"F32.imprint","IMPRINT",EDGE,{"derivedFrom":sQuery(id+"F32.wireOp",EDGE,"E69")}),1.0]])]});
            extrude(context, id + "F33", {"entities" : qUnion([Q0]), "operationType" : NewBodyOperationType.REMOVE, "oppositeDirection" : true, "depth" : 5 * mm, "offsetDistance" : 25 * mm});
        }
    });
